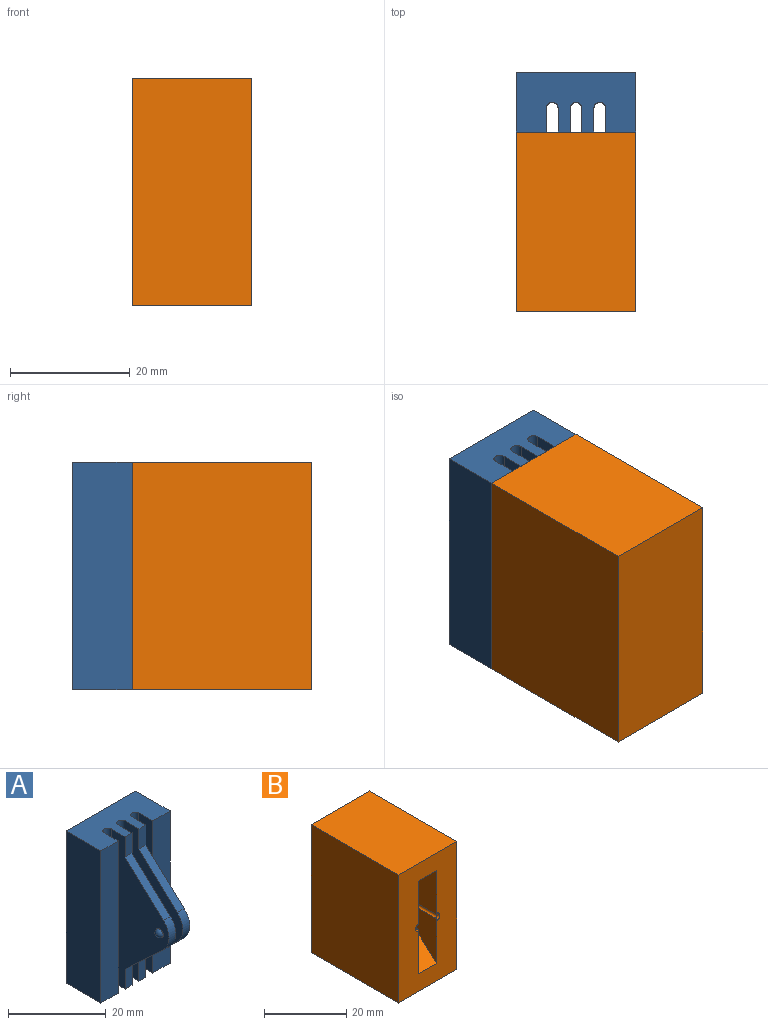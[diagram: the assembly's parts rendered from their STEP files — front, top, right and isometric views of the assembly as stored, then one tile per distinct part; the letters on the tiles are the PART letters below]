
ASSEMBLY  parts=2 mates=1
PART A: 28 faces, bbox 20x22.7x38 mm
  f0: plane 20x10mm, normal (0,0,1), area 171.3mm2, adj f3,f4,f6,f10,f11,f12,f13,f16
  f1: plane 20x10mm, normal (0,0,-1), area 171.3mm2, adj f2,f4,f5,f6,f10,f11,f13,f16
  f2: plane 5x2mm, normal (0,-1,0), area 10mm2, adj f1,f8,f16,f21
  f3: plane 5x2mm, normal (0,-1,0), area 10mm2, adj f0,f7,f16,f21
  f4: plane 38x5mm, normal (0,-1,0), area 190mm2, adj f0,f1,f11,f23
  f5: plane 5x2mm, normal (0,-1,0), area 10mm2, adj f1,f15,f17,f22
  f6: plane 38x5mm, normal (0,-1,0), area 190mm2, adj f0,f1,f10,f24
  f7: plane 11.08x10.34mm, normal (0,-0.68,0.73), area 30.3mm2, adj f3,f9,f16,f21
  f8: plane 11.08x10.34mm, normal (0,-0.68,-0.73), area 30.3mm2, adj f2,f9,f16,f21
  f9: cylinder r=5mm len=7.31mm, axis (-1,0,0), area 16.4mm2, adj f7,f8,f16,f21
  f10: plane 38x10mm, normal (1,0,0), area 380mm2, adj f0,f1,f6,f13
  f11: plane 38x10mm, normal (-1,0,0), area 380mm2, adj f0,f1,f4,f13
  f12: plane 5x2mm, normal (0,-1,0), area 10mm2, adj f0,f14,f17,f22
  f13: plane 38x20mm, normal (0,1,0), area 760mm2, adj f0,f1,f10,f11
  f14: plane 11.08x10.34mm, normal (0,-0.68,0.73), area 30.3mm2, adj f12,f17,f18,f22
  f15: plane 11.08x10.34mm, normal (0,-0.68,-0.73), area 30.3mm2, adj f5,f17,f18,f22
  f16: plane 38x16.67mm, normal (1,0,0), area 352.6mm2, adj f0,f1,f2,f3,f7,f8,f9,f19
  f17: plane 38x16.67mm, normal (-1,0,0), area 352.6mm2, adj f0,f1,f5,f12,f14,f15,f18,f20
  f18: cylinder r=5mm len=7.31mm, axis (-1,0,0), area 16.4mm2, adj f14,f15,f17,f22
  f19: sphere r=1mm, area 6.3mm2, adj f16
  f20: sphere r=1mm, area 6.3mm2, adj f17
  f21: plane 38x16.67mm, normal (-1,0,0), area 355.7mm2, adj f0,f1,f2,f3,f7,f8,f9,f27
  f22: plane 38x16.67mm, normal (1,0,0), area 355.7mm2, adj f0,f1,f5,f12,f14,f15,f18,f27
  f23: plane 38x4mm, normal (1,0,0), area 152mm2, adj f0,f1,f4,f26
  f24: plane 38x4mm, normal (-1,0,0), area 152mm2, adj f0,f1,f6,f25
  f25: cylinder r=1mm len=38mm, axis (0,0,1), area 119.4mm2, adj f0,f1,f16,f24
  f26: cylinder r=1mm len=38mm, axis (0,0,1), area 119.4mm2, adj f0,f1,f17,f23
  f27: cylinder r=1mm len=38mm, axis (0,0,1), area 119.4mm2, adj f0,f1,f21,f22
PART B: 25 faces, bbox 20x30x38 mm
  f0: plane 27.6x12.67mm, normal (1,0,0), area 187.8mm2, adj f1,f7,f9,f10,f12,f20,f21,f23
  f1: cylinder r=1.1mm len=2.2mm, axis (1,0,0), area 0.5mm2, adj f0,f2,f21,f23
  f2: sphere r=1.1mm, area 6.7mm2, adj f1,f22
  f3: plane 38x30mm, normal (1,0,0), area 1140mm2, adj f4,f6,f7,f8
  f4: plane 30x20mm, normal (0,0,1), area 600mm2, adj f3,f5,f7,f8
  f5: plane 38x30mm, normal (-1,0,0), area 1140mm2, adj f4,f6,f7,f8
  f6: plane 30x20mm, normal (0,0,-1), area 600mm2, adj f3,f5,f7,f8
  f7: plane 38x20mm, normal (0,-1,0), area 585.1mm2, adj f0,f3,f4,f5,f6,f9,f10,f11
  f8: plane 38x20mm, normal (0,1,0), area 760mm2, adj f3,f4,f5,f6
  f9: plane 10.96x9.95mm, normal (0,-0.67,-0.74), area 91.8mm2, adj f0,f7,f11,f12
  f10: plane 10.96x9.95mm, normal (0,-0.67,0.74), area 91.8mm2, adj f0,f7,f11,f12
  f11: plane 27.6x12.67mm, normal (-1,0,0), area 187.8mm2, adj f7,f9,f10,f12,f13,f15,f16,f18
  f12: cylinder r=5.2mm len=7.7mm, axis (-1,0,0), area 53.8mm2, adj f0,f9,f10,f11
  f13: cylinder r=1.1mm len=2.2mm, axis (-1,0,0), area 0.5mm2, adj f11,f14,f16,f18
  f14: sphere r=1.1mm, area 6.7mm2, adj f13,f17
  f15: cylinder r=0.6mm len=8.34mm, axis (0,-1,0), area 15.6mm2, adj f11,f16,f17,f18,f19
  f16: bspline ~0.42x0.41mm, area 0mm2, adj f11,f13,f15,f17
  f17: bspline ~1.51x0.87mm, area 0.8mm2, adj f14,f15,f16,f18
  f18: bspline ~0.42x0.41mm, area 0mm2, adj f11,f13,f15,f17
  f19: torus R=1.1mm, axis (0,-1,0), area 1.9mm2, adj f7,f11,f15
  f20: cylinder r=0.6mm len=8.34mm, axis (0,-1,0), area 15.6mm2, adj f0,f21,f22,f23,f24
  f21: bspline ~0.42x0.41mm, area 0mm2, adj f0,f1,f20,f22
  f22: bspline ~1.51x0.87mm, area 0.8mm2, adj f2,f20,f21,f23
  f23: bspline ~0.42x0.41mm, area 0mm2, adj f0,f1,f20,f22
  f24: torus R=1.1mm, axis (0,-1,0), area 1.9mm2, adj f0,f7,f20
PLACE A t=(-24.37,-4.94,17.53)mm
PLACE B rot(axis=(0,0,1),180deg) t=(-24.37,-44.94,17.53)mm fixed
MATE slider B.f7 <-> A.f6  axis (0,1,0) through (-14.37,-14.94,-1.47)mm
